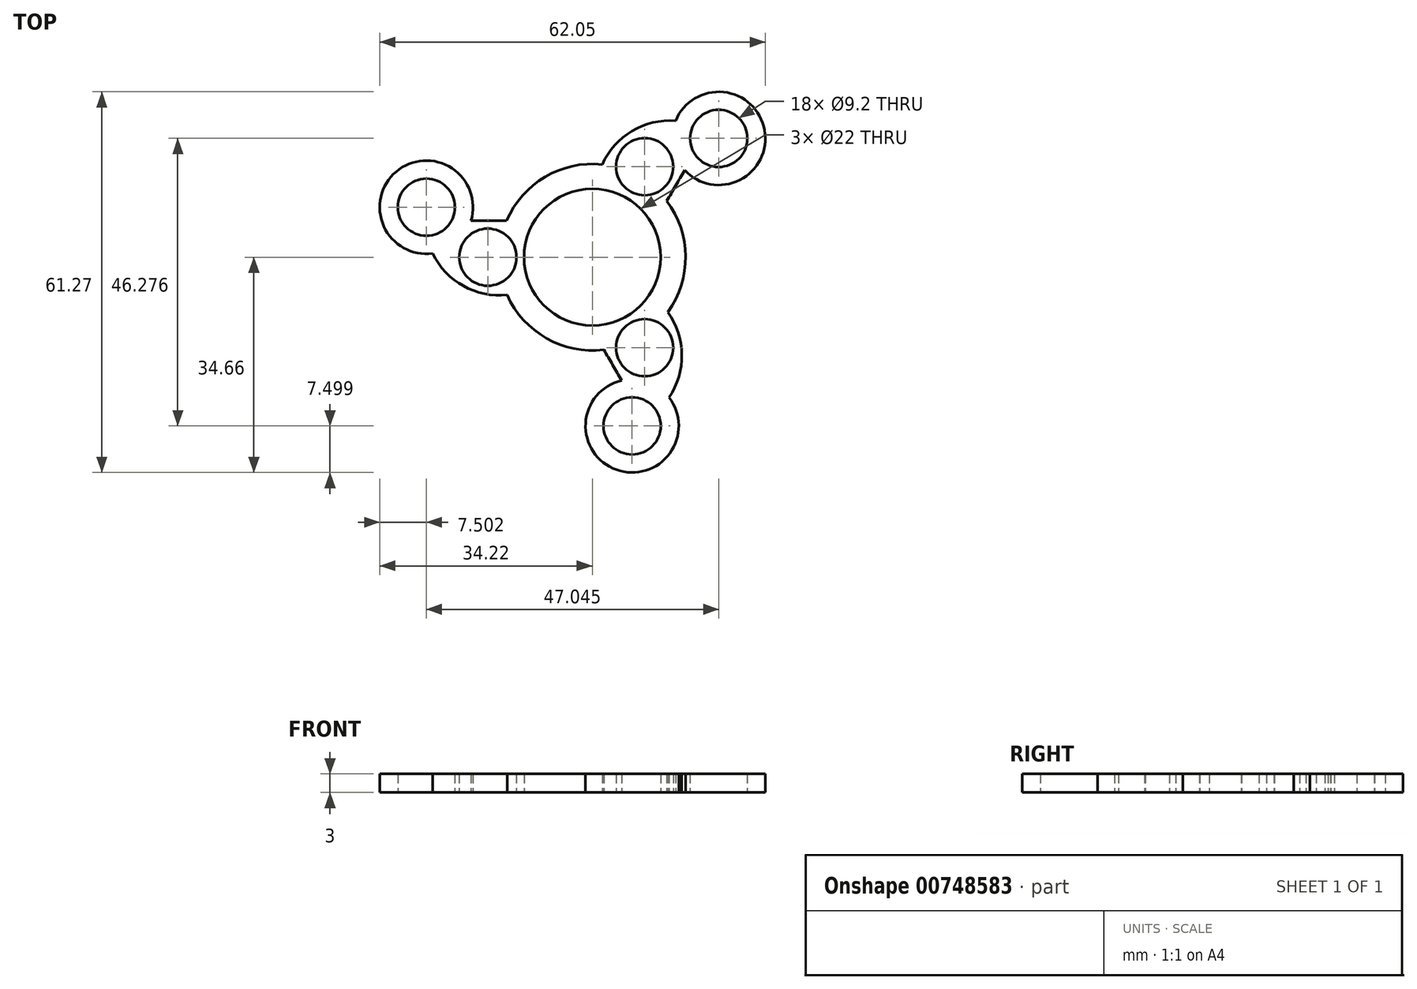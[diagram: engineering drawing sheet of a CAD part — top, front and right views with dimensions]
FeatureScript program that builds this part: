
annotation { "Feature Type Name" : "Feature", "Feature Type Description" : "" }
export const myFeature = defineFeature(function(context is Context, id is Id, definition is map)
    precondition{}
    {
        {
            var Q0;
            Q0=qCreatedBy(makeId("Top.planeOp"),FACE);
            var sketch = newSketch(context, id + "F0", { "sketchPlane" : qUnion([Q0])});
            skCircle(sketch, "E0", {"center": v(0, 0) * mm, "radius": 11 * mm});
            skArc(sketch, "E1", {"start": v(-13.7, -6.09) * mm, "mid": v(-7.4, -13.05) * mm, "end": v(1.83, -14.89) * mm});
            skArc(sketch, "E2", {"start": v(13.39, 21.97) * mm, "mid": v(6.38, 20.3) * mm, "end": v(1.58, 14.92) * mm});
            skArc(sketch, "E3", {"start": v(14.85, 14) * mm, "mid": v(27.7, 20.46) * mm, "end": v(13.39, 21.97) * mm});
            skCircle(sketch, "E4", {"center": v(20.33, 19.11) * mm, "radius": 4.6 * mm});
            skArc(sketch, "E5", {"start": v(14.85, 14) * mm, "mid": v(13.4, 11.52) * mm, "end": v(11.98, 9.03) * mm});
            skArc(sketch, "E6.1.0", {"start": v(-19.54, 5.86) * mm, "mid": v(-31.57, 13.76) * mm, "end": v(-25.72, 0.61) * mm});
            skCircle(sketch, "E6.1.1", {"center": v(-26.72, 8.05) * mm, "radius": 4.6 * mm});
            skArc(sketch, "E6.1.2", {"start": v(-19.54, 5.86) * mm, "mid": v(-16.68, 5.85) * mm, "end": v(-13.8, 5.86) * mm});
            skArc(sketch, "E6.1.3", {"start": v(-25.72, 0.61) * mm, "mid": v(-20.77, -4.63) * mm, "end": v(-13.7, -6.09) * mm});
            skArc(sketch, "E6.2.0", {"start": v(4.7, -19.86) * mm, "mid": v(3.87, -34.23) * mm, "end": v(12.33, -22.58) * mm});
            skCircle(sketch, "E6.2.1", {"center": v(6.4, -27.16) * mm, "radius": 4.6 * mm});
            skArc(sketch, "E6.2.2", {"start": v(4.7, -19.86) * mm, "mid": v(3.27, -17.37) * mm, "end": v(1.83, -14.89) * mm});
            skArc(sketch, "E6.2.3", {"start": v(12.33, -22.58) * mm, "mid": v(14.4, -15.67) * mm, "end": v(12.13, -8.83) * mm});
            skArc(sketch, "E7.trimOffspring", {"start": v(1.58, 14.92) * mm, "mid": v(-7.6, 12.93) * mm, "end": v(-13.8, 5.86) * mm});
            skLineSegment(sketch, "E8", {"start": v(-14.92, 5.85) * mm, "end": v(-16.82, 0) * mm});
            skCircle(sketch, "E9", {"center": v(-16.82, 0) * mm, "radius": 4.6 * mm});
            skCircle(sketch, "E10.1.0", {"center": v(8.41, -14.57) * mm, "radius": 4.6 * mm});
            skCircle(sketch, "E10.2.0", {"center": v(8.41, 14.57) * mm, "radius": 4.6 * mm});
            skArc(sketch, "E11.trimOffspring", {"start": v(12.13, -8.83) * mm, "mid": v(15, 0.13) * mm, "end": v(11.98, 9.03) * mm});
            skSolve(sketch);
        }
        {
            var Q0;
            Q0 = qSketchRegion(id + "F0", true);
            extrude(context, id + "F1", {"entities" : qUnion([Q0]), "depth" : 3 * mm, "offsetDistance" : 25 * mm});
        }
    });
